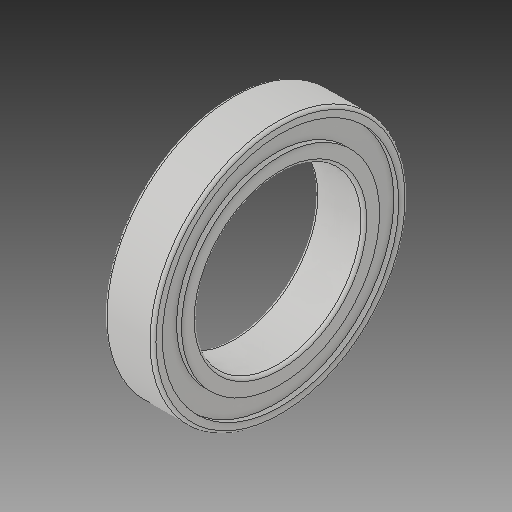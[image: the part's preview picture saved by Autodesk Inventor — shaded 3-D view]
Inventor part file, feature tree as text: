
AUTODESK INVENTOR PART (.ipt)
format: ipt  version: 2019 (Build 230136000, 136)  size: 177,664 bytes
history: native  units: in
note: dims shown in document units (in); Inventor stores cm internally (conversion verified against a paired STEP export)
features: fillet x1
ambient origin geometry x8: Origin, YZ Plane, XZ Plane, XY Plane, X Axis, Y Axis, Z Axis, Center Point
bodies: Solid1 (feature_tree)
feature tree (1):
  fillet  "Fillet1"  [1 undecoded]
note: 1 required parameter value undecoded (feature->parameter linkage not recoverable at this tier; creation-order binding heuristic only, values carry confidence <= 0.55)
